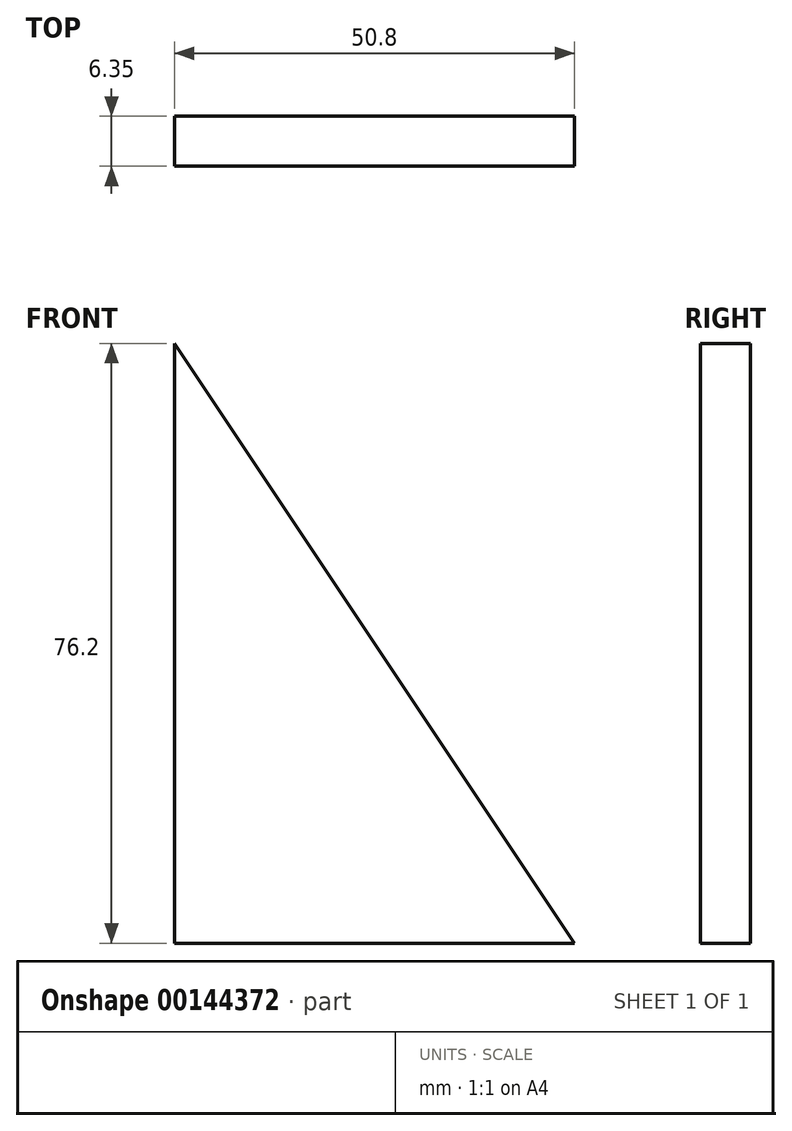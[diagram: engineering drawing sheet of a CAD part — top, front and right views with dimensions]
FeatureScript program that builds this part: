
annotation { "Feature Type Name" : "Feature", "Feature Type Description" : "" }
export const myFeature = defineFeature(function(context is Context, id is Id, definition is map)
    precondition{}
    {
        {
            var Q0;
            Q0=qCreatedBy(makeId("Front.planeOp"),FACE);
            var sketch = newSketch(context, id + "F0", { "sketchPlane" : qUnion([Q0])});
            skLineSegment(sketch, "E0", {"start": v(0, 76.2) * mm, "end": v(0, 0) * mm});
            skLineSegment(sketch, "E1", {"start": v(0, 0) * mm, "end": v(50.8, 0) * mm});
            skLineSegment(sketch, "E2", {"start": v(50.8, 0) * mm, "end": v(0, 76.2) * mm});
            skSolve(sketch);
        }
        {
            var Q0;
            Q0=makeQuery(id+"F0.imprint","IMPRINT",FACE,{"disambiguationData":[TD([[makeQuery(id+"F0.imprint","IMPRINT",EDGE,{"derivedFrom":sQuery(id+"F0.wireOp",EDGE,"E0")}),1.0]])]});
            extrude(context, id + "F1", {"entities" : qUnion([Q0]), "depth" : 6.35 * mm});
        }
    });
